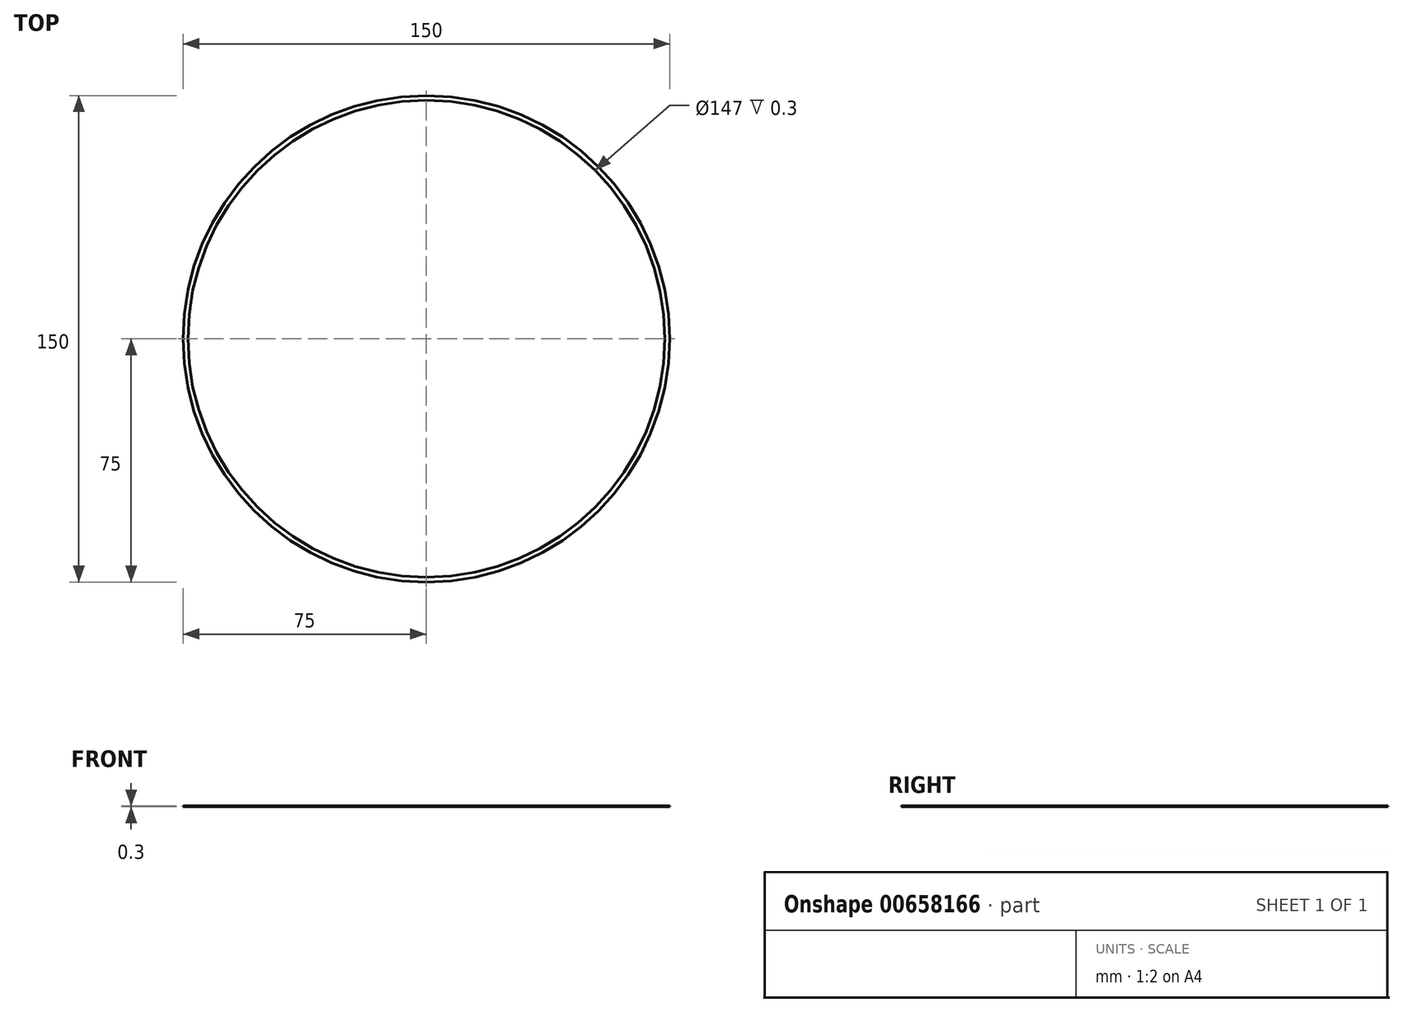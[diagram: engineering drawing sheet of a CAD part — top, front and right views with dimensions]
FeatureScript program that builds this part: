
annotation { "Feature Type Name" : "Feature", "Feature Type Description" : "" }
export const myFeature = defineFeature(function(context is Context, id is Id, definition is map)
    precondition{}
    {
        {
            var Q0;
            Q0=qCreatedBy(makeId("Top.planeOp"),FACE);
            var sketch = newSketch(context, id + "F0", { "sketchPlane" : qUnion([Q0])});
            skCircle(sketch, "E0", {"center": v(0, 0) * mm, "radius": 75 * mm});
            skCircle(sketch, "E1", {"center": v(0, 0) * mm, "radius": 73.5 * mm});
            skSolve(sketch);
        }
        {
            var Q0;
            Q0=makeQuery(id+"F0.imprint","IMPRINT",FACE,{"disambiguationData":[TD([[makeQuery(id+"F0.imprint","IMPRINT",EDGE,{"derivedFrom":sQuery(id+"F0.wireOp",EDGE,"E0")}),1.0]])]});
            extrude(context, id + "F1", {"entities" : qUnion([Q0]), "depth" : 0.3 * mm, "offsetDistance" : 25 * mm});
        }
    });
